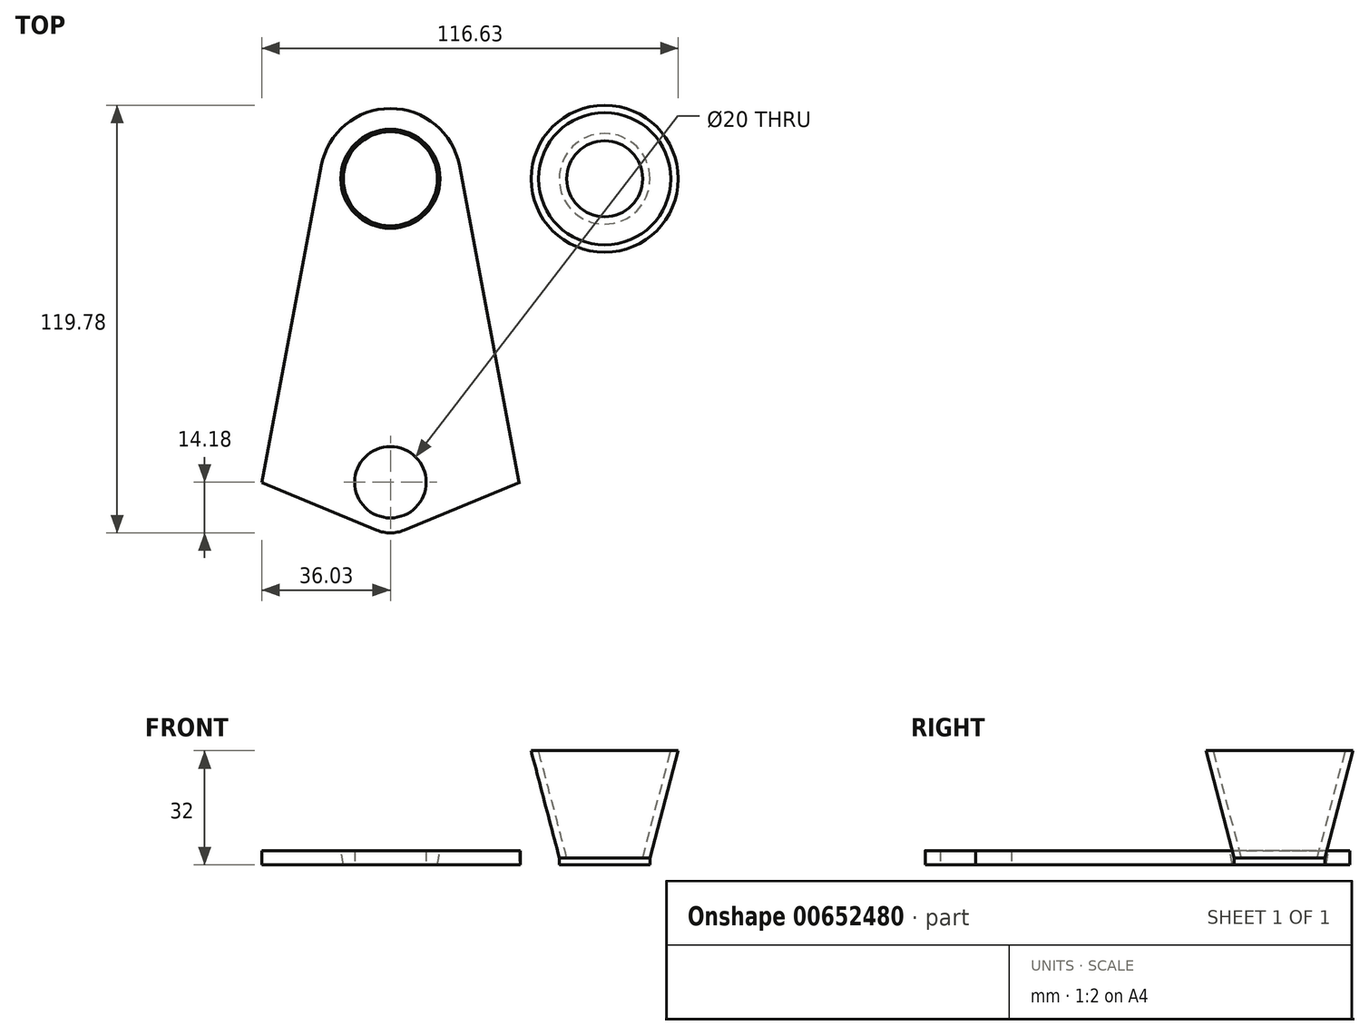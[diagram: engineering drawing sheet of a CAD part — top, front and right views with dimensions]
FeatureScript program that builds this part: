
annotation { "Feature Type Name" : "Feature", "Feature Type Description" : "" }
export const myFeature = defineFeature(function(context is Context, id is Id, definition is map)
    precondition{}
    {
        {
            var Q0;
            Q0=qCreatedBy(makeId("Top.planeOp"),FACE);
            var sketch = newSketch(context, id + "F0", { "sketchPlane" : qUnion([Q0])});
            skCircle(sketch, "E0.cCircle", {"center": v(0, 0) * mm, "radius": 85 * mm, "construction": true});
            skLineSegment(sketch, "E0.0", {"start": v(92.07, 8.28) * mm, "end": v(69.61, -60.82) * mm});
            skLineSegment(sketch, "E0.1", {"start": v(36.33, -85) * mm, "end": v(-36.33, -85) * mm});
            skLineSegment(sketch, "E0.2", {"start": v(-69.61, -60.82) * mm, "end": v(-92.07, 8.28) * mm});
            skLineSegment(sketch, "E0.3", {"start": v(-79.35, 47.41) * mm, "end": v(-20.57, 90.12) * mm});
            skLineSegment(sketch, "E0.4", {"start": v(20.57, 90.12) * mm, "end": v(79.35, 47.41) * mm});
            skPoint(sketch, "E0.0.midPoint", {"position": v(80.84, -26.27) * mm});
            skPoint(sketch, "E1.visualSharp", {"position": v(-99.92, 32.47) * mm});
            skArc(sketch, "E1.filletArc", {"start": v(-79.35, 47.41) * mm, "mid": v(-92.07, 29.91) * mm, "end": v(-92.07, 8.28) * mm});
            skPoint(sketch, "E2.visualSharp", {"position": v(-61.76, -85) * mm});
            skArc(sketch, "E2.filletArc", {"start": v(-69.61, -60.82) * mm, "mid": v(-56.9, -78.32) * mm, "end": v(-36.33, -85) * mm});
            skPoint(sketch, "E3.visualSharp", {"position": v(61.76, -85) * mm});
            skArc(sketch, "E3.filletArc", {"start": v(36.33, -85) * mm, "mid": v(56.9, -78.32) * mm, "end": v(69.61, -60.82) * mm});
            skPoint(sketch, "E4.visualSharp", {"position": v(99.92, 32.47) * mm});
            skArc(sketch, "E4.filletArc", {"start": v(92.07, 8.28) * mm, "mid": v(92.07, 29.91) * mm, "end": v(79.35, 47.41) * mm});
            skPoint(sketch, "E5.visualSharp", {"position": v(0, 105.07) * mm});
            skArc(sketch, "E5.filletArc", {"start": v(20.57, 90.12) * mm, "mid": v(0, 96.8) * mm, "end": v(-20.57, 90.12) * mm});
            skArc(sketch, "E6.0", {"start": v(89.21, 9.2) * mm, "mid": v(89.21, 28.99) * mm, "end": v(77.59, 44.99) * mm});
            skLineSegment(sketch, "E6.1", {"start": v(18.8, 87.7) * mm, "end": v(77.59, 44.99) * mm});
            skLineSegment(sketch, "E6.2", {"start": v(89.21, 9.2) * mm, "end": v(66.76, -59.89) * mm});
            skArc(sketch, "E6.3", {"start": v(18.8, 87.7) * mm, "mid": v(0, 93.8) * mm, "end": v(-18.8, 87.7) * mm});
            skLineSegment(sketch, "E6.4", {"start": v(-77.59, 44.99) * mm, "end": v(-18.8, 87.7) * mm});
            skArc(sketch, "E6.5", {"start": v(-77.59, 44.99) * mm, "mid": v(-89.21, 28.99) * mm, "end": v(-89.21, 9.2) * mm});
            skArc(sketch, "E6.6", {"start": v(36.33, -82) * mm, "mid": v(55.14, -75.89) * mm, "end": v(66.76, -59.89) * mm});
            skLineSegment(sketch, "E6.7", {"start": v(36.33, -82) * mm, "end": v(-36.33, -82) * mm});
            skArc(sketch, "E6.8", {"start": v(-66.76, -59.89) * mm, "mid": v(-55.14, -75.89) * mm, "end": v(-36.33, -82) * mm});
            skLineSegment(sketch, "E6.9", {"start": v(-66.76, -59.89) * mm, "end": v(-89.21, 9.2) * mm});
            skCircle(sketch, "E7", {"center": v(-90.26, 29.33) * mm, "radius": 0.9 * mm});
            skCircle(sketch, "E8", {"center": v(79.03, -25.68) * mm, "radius": 0.9 * mm});
            skPoint(sketch, "E9", {"position": v(-89.21, 28.99) * mm});
            skLineSegment(sketch, "E10.0", {"start": v(-89.21, 28.99) * mm, "end": v(-90.26, 29.33) * mm, "construction": true});
            skLineSegment(sketch, "E11.0", {"start": v(80.84, -26.27) * mm, "end": v(0, 0) * mm, "construction": true});
            skArc(sketch, "E12", {"start": v(19.66, 3.7) * mm, "mid": v(0, 20) * mm, "end": v(-19.66, 3.7) * mm});
            skLineSegment(sketch, "E13", {"start": v(-19.66, 3.7) * mm, "end": v(-36.33, -85) * mm});
            skLineSegment(sketch, "E14", {"start": v(19.66, 3.7) * mm, "end": v(36.33, -85) * mm});
            skLineSegment(sketch, "E15.0", {"start": v(-19.36, 3.64) * mm, "end": v(-36.03, -85.06) * mm});
            skArc(sketch, "E15.1", {"start": v(19.36, 3.64) * mm, "mid": v(0, 19.7) * mm, "end": v(-19.36, 3.64) * mm});
            skLineSegment(sketch, "E15.2", {"start": v(19.36, 3.64) * mm, "end": v(36.03, -85.06) * mm});
            skLineSegment(sketch, "E16", {"start": v(-36.03, -85.06) * mm, "end": v(-3.82, -98.41) * mm});
            skLineSegment(sketch, "E17", {"start": v(3.83, -98.42) * mm, "end": v(36.33, -85) * mm});
            skCircle(sketch, "E18", {"center": v(0, -85) * mm, "radius": 10 * mm});
            skPoint(sketch, "E19.visualSharp", {"position": v(0, -100) * mm});
            skArc(sketch, "E19.filletArc", {"start": v(-3.82, -98.41) * mm, "mid": v(0, -99.18) * mm, "end": v(3.83, -98.42) * mm});
            skCircle(sketch, "E20", {"center": v(0, 0) * mm, "radius": 13 * mm});
            skSolve(sketch);
        }
        {
            var Q0;
            {var subQ0=sQuery(id+"F0.wireOp",EDGE,"E15.0");var subQ1=sQuery(id+"F0.wireOp",EDGE,"E0.1");var subQ2=makeQuery(id+"F0.imprint","INTERSECT",VERTEX,{"derivedFrom":[subQ1,subQ0]});Q0=makeQuery(id+"F0.imprint","IMPRINT",FACE,{"disambiguationData":[TD([[makeQuery(id+"F0.imprint","IMPRINT",EDGE,{"disambiguationData":[TD([[subQ2,1.0]])],"derivedFrom":subQ1}),-1.0]])]});}
            var Q1;
            {var subQ0=sQuery(id+"F0.wireOp",EDGE,"E15.2");var subQ1=sQuery(id+"F0.wireOp",EDGE,"E0.1");var subQ2=makeQuery(id+"F0.imprint","INTERSECT",VERTEX,{"derivedFrom":[subQ1,subQ0]});Q1=makeQuery(id+"F0.imprint","IMPRINT",FACE,{"disambiguationData":[TD([[makeQuery(id+"F0.imprint","IMPRINT",EDGE,{"disambiguationData":[TD([[subQ2,-1.0]])],"derivedFrom":subQ1}),-1.0]])]});}
            var Q2;
            {var subQ0=sQuery(id+"F0.wireOp",EDGE,"E15.1");Q2=makeQuery(id+"F0.imprint","IMPRINT",FACE,{"disambiguationData":[TD([[makeQuery(id+"F0.imprint","IMPRINT",EDGE,{"derivedFrom":subQ0}),1.0]])]});}
            var Q3;
            {var subQ0=sQuery(id+"F0.wireOp",EDGE,"E16");Q3=makeQuery(id+"F0.imprint","IMPRINT",FACE,{"disambiguationData":[TD([[makeQuery(id+"F0.imprint","IMPRINT",EDGE,{"derivedFrom":subQ0}),1.0]])]});}
            extrude(context, id + "F1", {"entities" : qUnion([Q0, Q1, Q2, Q3]), "depth" : 4 * mm, "offsetDistance" : 25 * mm});
        }
        {
            var Q0;
            Q0=qCreatedBy(makeId("Front.planeOp"),FACE);
            var sketch = newSketch(context, id + "F2", { "sketchPlane" : qUnion([Q0])});
            skLineSegment(sketch, "E21", {"start": v(60, 0) * mm, "end": v(60, 25.28) * mm, "construction": true});
            skLineSegment(sketch, "E22", {"start": v(60, 0) * mm, "end": v(72.7, 0) * mm});
            skLineSegment(sketch, "E23", {"start": v(72.7, 0) * mm, "end": v(72.7, 2) * mm});
            skLineSegment(sketch, "E24", {"start": v(72.7, 2) * mm, "end": v(80.6, 32) * mm});
            skLineSegment(sketch, "E25", {"start": v(80.6, 32) * mm, "end": v(78.53, 32) * mm});
            skLineSegment(sketch, "E26", {"start": v(78.53, 32) * mm, "end": v(70.63, 2) * mm});
            skLineSegment(sketch, "E27", {"start": v(70.63, 2) * mm, "end": v(60, 2) * mm});
            skLineSegment(sketch, "E28", {"start": v(60, 2) * mm, "end": v(60, 0) * mm});
            skSolve(sketch);
        }
        {
            var Q0;
            Q0 = qSketchRegion(id + "F2", true);
            var Q1;
            Q1=sQuery(id+"F2.wireOp",EDGE,"E21");
            revolve(context, id + "F3", {"surfaceOperationType" : NewSurfaceOperationType.NEW, "entities" : qUnion([Q0]), "axis" : qUnion([Q1]), "revolveType" : RevolveType.FULL});
        }
        {
            var Q0;
            Q0=makeQuery(id+"F1.opExtrude","CAP_EDGE",EDGE,{"disambiguationData":[OSD([sQuery(id+"F0.wireOp",EDGE,"E20")])],"isStart":false});
            chamfer(context, id + "F4", {"entities" : qUnion([Q0]), "chamferType" : ChamferType.OFFSET_ANGLE, "width" : 5 * mm, "oppositeDirection" : false, "angle" : 10 * degree, "tangentPropagation" : true});
        }
    });
